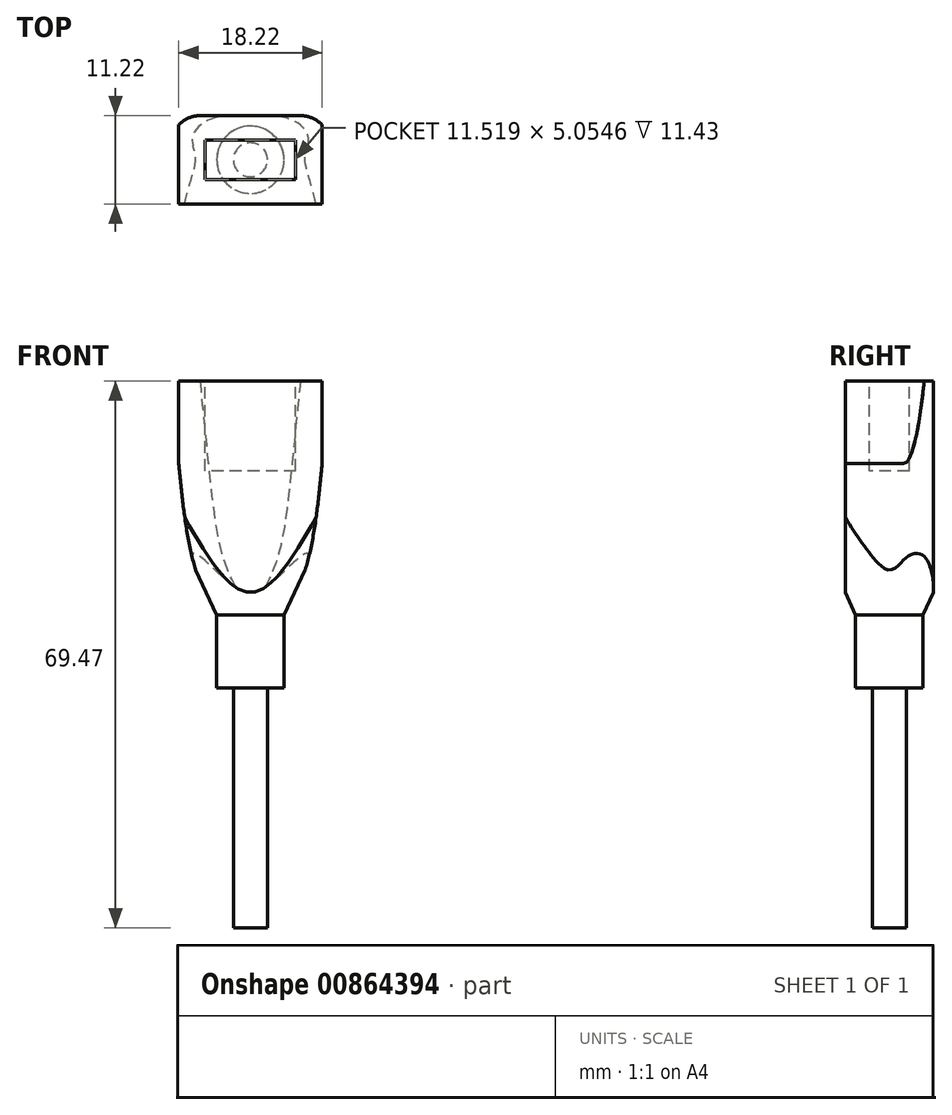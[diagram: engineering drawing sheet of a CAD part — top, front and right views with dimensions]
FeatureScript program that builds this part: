
annotation { "Feature Type Name" : "Feature", "Feature Type Description" : "" }
export const myFeature = defineFeature(function(context is Context, id is Id, definition is map)
    precondition{}
    {
        {
            var Q0;
            Q0=qCreatedBy(makeId("Front.planeOp"),FACE);
            var sketch = newSketch(context, id + "F0", { "sketchPlane" : qUnion([Q0])});
            skLineSegment(sketch, "E0.bottom", {"start": v(9.11, 14.86) * mm, "end": v(-9.11, 14.86) * mm});
            skLineSegment(sketch, "E0.top", {"start": v(9.11, -14.86) * mm, "end": v(-9.11, -14.86) * mm});
            skLineSegment(sketch, "E0.left", {"start": v(9.11, 14.86) * mm, "end": v(9.11, -14.86) * mm});
            skLineSegment(sketch, "E0.right", {"start": v(-9.11, 14.86) * mm, "end": v(-9.11, -14.86) * mm});
            skPoint(sketch, "E0.middle", {"position": v(0, 0) * mm});
            skSolve(sketch);
        }
        {
            var Q0;
            Q0 = qSketchRegion(id + "F0", true);
            extrude(context, id + "F1", {"entities" : qUnion([Q0]), "endBound" : BoundingType.SYMMETRIC, "depth" : 11.21 * mm, "offsetDistance" : 25.4 * mm});
        }
        {
            var Q0;
            Q0=makeQuery(id+"F1.opExtrude","CAP_FACE",FACE,{"disambiguationData":[OSD([sQuery(id+"F0.wireOp",EDGE,"E0.bottom"),sQuery(id+"F0.wireOp",EDGE,"E0.top"),sQuery(id+"F0.wireOp",EDGE,"E0.left"),sQuery(id+"F0.wireOp",EDGE,"E0.right")])],"isStart":false});
            var sketch = newSketch(context, id + "F2", { "sketchPlane" : qUnion([Q0])});
            skLineSegment(sketch, "E1.bottom", {"start": v(-9.11, 14.86) * mm, "end": v(9.11, 14.86) * mm});
            skLineSegment(sketch, "E1.top", {"start": v(-9.11, 4.36) * mm, "end": v(9.11, 4.36) * mm});
            skLineSegment(sketch, "E1.left", {"start": v(-9.11, 14.86) * mm, "end": v(-9.11, 4.36) * mm});
            skLineSegment(sketch, "E1.right", {"start": v(9.11, 14.86) * mm, "end": v(9.11, 4.36) * mm});
            skCircle(sketch, "E2", {"center": v(0, -14.86) * mm, "radius": 4.28 * mm});
            skLineSegment(sketch, "E3", {"start": v(0, -14.86) * mm, "end": v(0, 1.77) * mm});
            skFitSpline(sketch, "E4", {"points": [v(4.28, -14.86) * mm, v(7.11, -8.61) * mm, v(9.11, 4.36) * mm], "startDerivative": vector(7.44, 13.32) * mm, "endDerivative": vector(2.5, 24.51) * mm});
            skFitSpline(sketch, "E5.MirrorCS", {"points": [v(-4.28, -14.86) * mm, v(-7.11, -8.61) * mm, v(-9.11, 4.36) * mm], "startDerivative": vector(-7.44, 13.32) * mm, "endDerivative": vector(-2.5, 24.51) * mm});
            skSolve(sketch);
        }
        {
            var Q0;
            {var subQ0=sQuery(id+"F2.wireOp",EDGE,"E5.MirrorCS");Q0=makeQuery(id+"F2.imprint","IMPRINT",FACE,{"disambiguationData":[TD([[makeQuery(id+"F2.imprint","IMPRINT",EDGE,{"derivedFrom":subQ0}),1.0]])]});}
            var Q1;
            {var subQ0=sQuery(id+"F2.wireOp",EDGE,"E4");Q1=makeQuery(id+"F2.imprint","IMPRINT",FACE,{"disambiguationData":[TD([[makeQuery(id+"F2.imprint","IMPRINT",EDGE,{"derivedFrom":subQ0}),-1.0]])]});}
            extrude(context, id + "F3", {"entities" : qUnion([Q0, Q1]), "operationType" : NewBodyOperationType.REMOVE, "oppositeDirection" : true, "depth" : 25.4 * mm, "offsetDistance" : 25.4 * mm});
        }
        {
            var Q0;
            Q0=makeQuery(id+"F3.boolean.opBoolean","COPY",EDGE,{"derivedFrom":makeQuery(id+"F3.opExtrude","CAP_EDGE",EDGE,{"disambiguationData":[OSD([sQuery(id+"F2.wireOp",EDGE,"E4")])],"isStart":true})});
            var Q1;
            Q1=makeQuery(id+"F3.boolean.opBoolean","INTERSECT",EDGE,{"derivedFrom":[makeQuery(id+"F1.opExtrude","CAP_FACE",FACE,{"disambiguationData":[OSD([sQuery(id+"F0.wireOp",EDGE,"E0.bottom"),sQuery(id+"F0.wireOp",EDGE,"E0.top"),sQuery(id+"F0.wireOp",EDGE,"E0.left"),sQuery(id+"F0.wireOp",EDGE,"E0.right")])],"isStart":true}),makeQuery(id+"F3.opExtrude","SWEPT_FACE",FACE,{"disambiguationData":[OSD([sQuery(id+"F2.wireOp",EDGE,"E4")])]})]});
            var Q2;
            Q2=makeQuery(id+"F3.boolean.opBoolean","INTERSECT",EDGE,{"derivedFrom":[makeQuery(id+"F1.opExtrude","CAP_FACE",FACE,{"disambiguationData":[OSD([sQuery(id+"F0.wireOp",EDGE,"E0.bottom"),sQuery(id+"F0.wireOp",EDGE,"E0.top"),sQuery(id+"F0.wireOp",EDGE,"E0.left"),sQuery(id+"F0.wireOp",EDGE,"E0.right")])],"isStart":true}),makeQuery(id+"F3.opExtrude","SWEPT_FACE",FACE,{"disambiguationData":[OSD([sQuery(id+"F2.wireOp",EDGE,"E5.MirrorCS")])]})]});
            var Q3;
            Q3=makeQuery(id+"F3.boolean.opBoolean","COPY",EDGE,{"derivedFrom":makeQuery(id+"F3.opExtrude","CAP_EDGE",EDGE,{"disambiguationData":[OSD([sQuery(id+"F2.wireOp",EDGE,"E5.MirrorCS")])],"isStart":true})});
            fillet(context, id + "F4", {"entities" : qUnion([Q0, Q1, Q2, Q3]), "radius" : 3.8 * mm, "tangentPropagation" : true, "allowEdgeOverflow" : false});
        }
        {
            var Q0;
            Q0=makeQuery(id+"F1.opExtrude","SWEPT_FACE",FACE,{"disambiguationData":[OSD([sQuery(id+"F0.wireOp",EDGE,"E0.top")])]});
            var sketch = newSketch(context, id + "F5", { "sketchPlane" : qUnion([Q0])});
            skCircle(sketch, "E6", {"center": v(0, 0) * mm, "radius": 4.28 * mm});
            skSolve(sketch);
        }
        {
            var Q0;
            Q0 = qSketchRegion(id + "F5", true);
            extrude(context, id + "F6", {"entities" : qUnion([Q0]), "operationType" : NewBodyOperationType.ADD, "depth" : 9.27 * mm, "offsetDistance" : 25.4 * mm});
        }
        {
            var Q0;
            {var subQ0=sQuery(id+"F2.wireOp",EDGE,"E4");var subQ1=sQuery(id+"F0.wireOp",EDGE,"E0.right");var subQ2=sQuery(id+"F0.wireOp",EDGE,"E0.left");var subQ3=sQuery(id+"F0.wireOp",EDGE,"E0.top");var subQ4=sQuery(id+"F0.wireOp",EDGE,"E0.bottom");var subQ6=makeQuery(id+"F1.opExtrude","SWEPT_FACE",FACE,{"disambiguationData":[OSD([subQ3])]});Q0=makeQuery(id+"F6.boolean.opBoolean","SPLIT",FACE,{"disambiguationData":[TD([makeQuery(id+"F4.opFillet","BLEND_FACE",FACE,{"disambiguationData":[OSD([subQ4,subQ3,subQ2,subQ1,subQ0])]})])],"derivedFrom":subQ6});}
            var sketch = newSketch(context, id + "F7", { "sketchPlane" : qUnion([Q0])});
            skCircle(sketch, "E7.0.0", {"center": v(0, 0) * mm, "radius": 4.28 * mm});
            skCircle(sketch, "E8.0", {"center": v(0, 0) * mm, "radius": 16.98 * mm});
            skSolve(sketch);
        }
        {
            var Q0;
            Q0 = qSketchRegion(id + "F7", true);
            extrude(context, id + "F8", {"entities" : qUnion([Q0]), "operationType" : NewBodyOperationType.REMOVE, "oppositeDirection" : true, "depth" : 12.7 * mm, "offsetDistance" : 25.4 * mm, "hasDraft" : true, "draftAngle" : 25 * degree, "draftPullDirection" : true});
        }
        {
            var Q0;
            Q0=makeQuery(id+"F6.opExtrude","CAP_FACE",FACE,{"disambiguationData":[OSD([sQuery(id+"F5.wireOp",EDGE,"E6")])],"isStart":false});
            var sketch = newSketch(context, id + "F9", { "sketchPlane" : qUnion([Q0])});
            skCircle(sketch, "E9", {"center": v(0, 0) * mm, "radius": 2.16 * mm});
            skSolve(sketch);
        }
        {
            var Q0;
            Q0 = qSketchRegion(id + "F9", true);
            extrude(context, id + "F10", {"entities" : qUnion([Q0]), "operationType" : NewBodyOperationType.ADD, "depth" : 30.48 * mm, "offsetDistance" : 25.4 * mm});
        }
        {
            var Q0;
            Q0=makeQuery(id+"F1.opExtrude","SWEPT_FACE",FACE,{"disambiguationData":[OSD([sQuery(id+"F0.wireOp",EDGE,"E0.bottom")])]});
            var sketch = newSketch(context, id + "F11", { "sketchPlane" : qUnion([Q0])});
            skLineSegment(sketch, "E10.bottom", {"start": v(5.76, 2.53) * mm, "end": v(-5.76, 2.53) * mm});
            skLineSegment(sketch, "E10.top", {"start": v(5.76, -2.53) * mm, "end": v(-5.76, -2.53) * mm});
            skLineSegment(sketch, "E10.left", {"start": v(5.76, 2.53) * mm, "end": v(5.76, -2.53) * mm});
            skLineSegment(sketch, "E10.right", {"start": v(-5.76, 2.53) * mm, "end": v(-5.76, -2.53) * mm});
            skPoint(sketch, "E10.middle", {"position": v(0, 0) * mm});
            skSolve(sketch);
        }
        {
            var Q0;
            Q0 = qSketchRegion(id + "F11", true);
            extrude(context, id + "F12", {"entities" : qUnion([Q0]), "operationType" : NewBodyOperationType.REMOVE, "oppositeDirection" : true, "depth" : 11.43 * mm, "offsetDistance" : 25.4 * mm});
        }
    });
